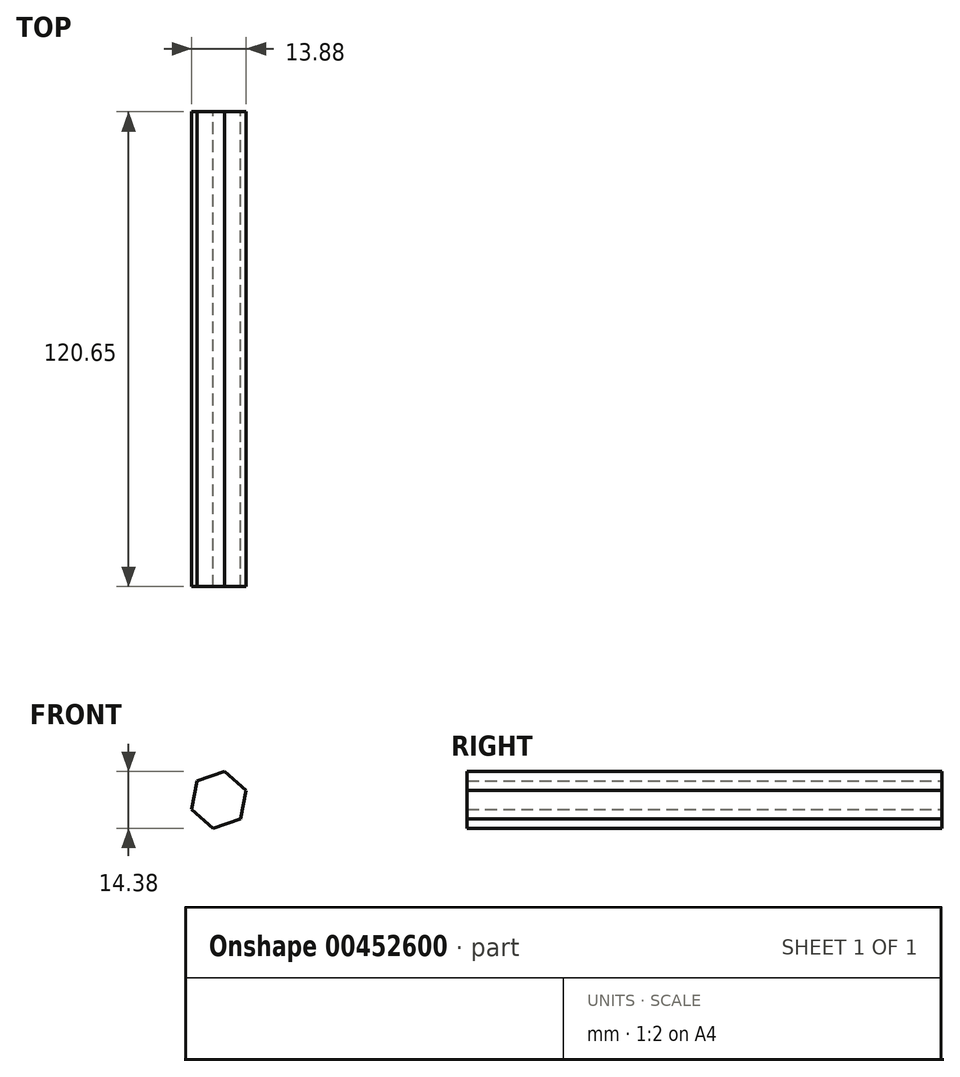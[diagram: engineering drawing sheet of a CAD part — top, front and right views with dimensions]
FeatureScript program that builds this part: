
annotation { "Feature Type Name" : "Feature", "Feature Type Description" : "" }
export const myFeature = defineFeature(function(context is Context, id is Id, definition is map)
    precondition{}
    {
        {
            var Q0;
            Q0=qCreatedBy(makeId("Front.planeOp"),FACE);
            var sketch = newSketch(context, id + "F0", { "sketchPlane" : qUnion([Q0])});
            skCircle(sketch, "E0.cCircle", {"center": v(0, 0) * mm, "radius": 6.35 * mm, "construction": true});
            skLineSegment(sketch, "E0.0", {"start": v(1.41, 7.2) * mm, "end": v(6.94, 2.37) * mm});
            skLineSegment(sketch, "E0.1", {"start": v(6.94, 2.37) * mm, "end": v(5.52, -4.82) * mm});
            skLineSegment(sketch, "E0.2", {"start": v(5.52, -4.82) * mm, "end": v(-1.41, -7.2) * mm});
            skLineSegment(sketch, "E0.3", {"start": v(-1.41, -7.2) * mm, "end": v(-6.94, -2.37) * mm});
            skLineSegment(sketch, "E0.4", {"start": v(-6.94, -2.37) * mm, "end": v(-5.52, 4.82) * mm});
            skLineSegment(sketch, "E0.5", {"start": v(-5.52, 4.82) * mm, "end": v(1.41, 7.2) * mm});
            skPoint(sketch, "E0.0.midPoint", {"position": v(4.18, 4.78) * mm});
            skSolve(sketch);
        }
        {
            var Q0;
            Q0=makeQuery(id+"F0.imprint","IMPRINT",FACE,{"disambiguationData":[TD([[makeQuery(id+"F0.imprint","IMPRINT",EDGE,{"derivedFrom":sQuery(id+"F0.wireOp",EDGE,"E0.0")}),-1.0]])]});
            extrude(context, id + "F1", {"entities" : qUnion([Q0]), "depth" : 120.65 * mm});
        }
    });
